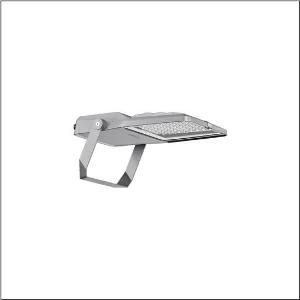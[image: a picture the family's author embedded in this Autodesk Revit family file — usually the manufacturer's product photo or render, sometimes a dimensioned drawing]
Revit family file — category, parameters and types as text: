
# Revit family: floodlight_fl_21_iq_mini___pl43_5xa7771c4a1a_6230
name_source: partatom
category: Lighting Fixtures
units: mm (PartAtom-declared; Revit-internal decimal feet)

## family parameters
Cut with Voids When Loaded = No
Host = Face
Light Source = No
Part Type = Normal
Room Calculation Point = No
Round Connector Dimension = Use Diameter
Shared = No

## types (1)
- --- (1 x LED, 13050 lm, 87.2 W, 4000K)
    Apparent Load = 87 VA
    CIE Flux Codes = 27 78 99 100 100
    Color Rendering = 70
    Color Temperature = 4000K
    Default Elevation = 1800 mm
    Description = Floodlight FL 21 iQ mini, floodlight, primary light control with lens, of PMMA, primary optical cover: protective disc, of toughened safety glass, transparent, light distribution: PL43, light emission: direct distribution, installation type: surface-mounted, LED, High Power LED, rated luminous flux: 13.050lm, luminous efficacy: 150lm/W, light colour: 740, colour temperature: 4000K, control: Auto-Match, Temp-Guard, Lumen-Switch, Night-Set, Smart-Wire, Light-Fading, Desk-Remote (wireless, voltage-free reading and setting of iQ features in the workshop via application-optimized NFC function/RFID function), optimised constant luminous flux control (CLO 2.0), with terminal, 6-pole, mains connection: 220..240V, AC, 50/60Hz, start of lifetime: 87W, end of service life: 92W, reduction: 40W, luminaire housing, of diecast aluminium, powder-coated, Siteco® metallic grey (DB 702S), corrosivity category C5 mid according to DIN EN ISO 12944, sealing non-destructively replaceable, mounting bracket, of steel, galvanised, powder-coated, Siteco® metallic grey (DB 702S), protection rating (complete): IP66, insulation class (complete): insulation class II (safety insulation), certification: CE, ENEC, VDE, protection symbol: D, impact resistance: IK08, permissible operating ambient temperature: -40..+40°C, permissible operating ambient temperature for outdoor applications: -40..+50°C, standard: DIN EN 12944, LABS conformity tested according to VDMA 24364:2018-05, packaging unit: 1 piece

Light Distribution: PL43
    Height = 70 mm
    Lamp = 1 x LED
    Lamp Light Flux = 13050 lm
    Lamp Power = 87.2 W
    Lamp count = 1
    Length = 485 mm
    Luminous efficacy = 150 lm/W
    Manufacturer = Siteco
    ModVariant = No
    Model = 5XA7771C4A1A
    Number of Poles = 1
    OnlyDefault = Yes
    Power Factor = 1
    Product Name = Floodlight FL 21 iQ mini | PL43
    Product group = floodlight | pylon annexe
    ProductGroupID = 6200
    Protection Class = Protection class II
    Protection Degree = IP 66
    RLX_Detail_Level = 1
    RLX_Emergency_Light_Flux = 0 lm
    RLX_Emergency_Type = 0
    RLX_Emergency_Type_DB = No
    RlxData = <blob elided: 96261 chars, md5=96c0183c>
    Socket = socket
    Standby Power = 0 W
    System Light Flux = 13050 lm
    System Power = 87 W
    Type Comments = factory setting: luminous flux: 100 % | dim-lin: 254 | 456 mA
    Type Image = l_1006845.jpg
    URL = http://relux.com
    VarID = @adj_094241
    Voltage = 0 V
    Weight = 0.00 kg
    Width = 337 mm

## geometry (parser evidence)
native form markers: Blend x4, Sweep x11
no freeform markers — native parametric forms only
